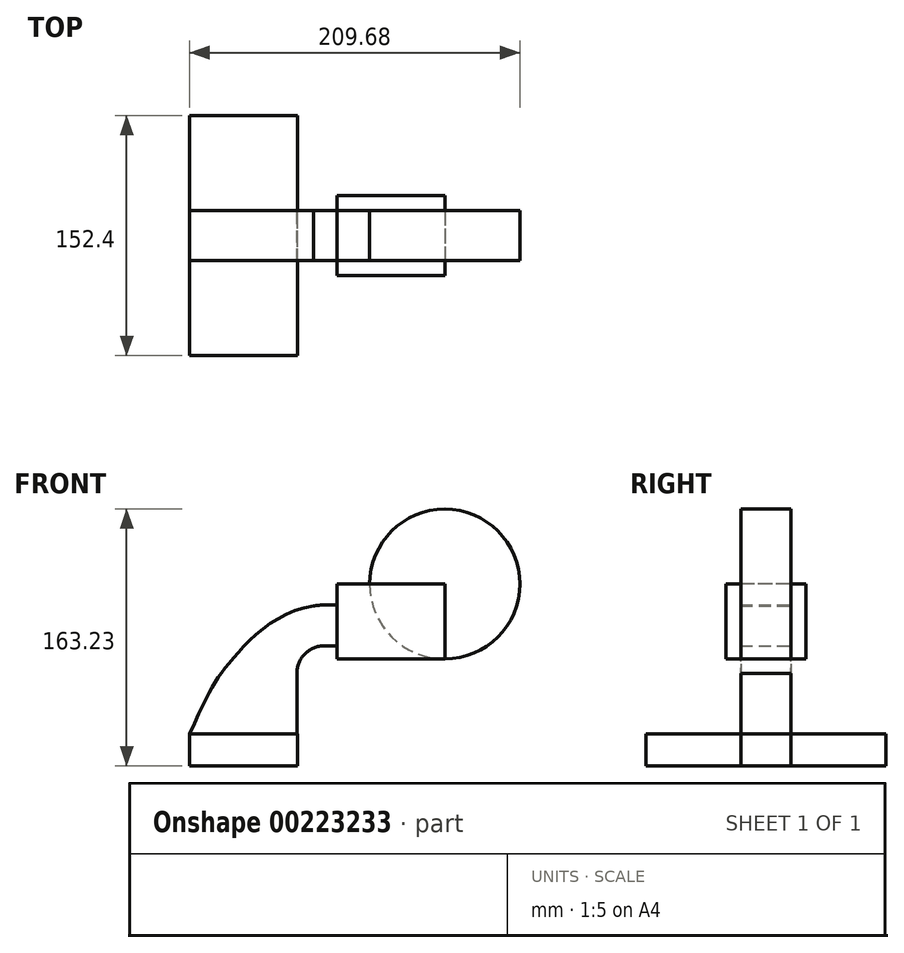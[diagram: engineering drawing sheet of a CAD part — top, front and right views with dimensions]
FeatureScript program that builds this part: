
annotation { "Feature Type Name" : "Feature", "Feature Type Description" : "" }
export const myFeature = defineFeature(function(context is Context, id is Id, definition is map)
    precondition{}
    {
        {
            var Q0;
            Q0=qCreatedBy(makeId("Front.planeOp"),FACE);
            var sketch = newSketch(context, id + "F0", { "sketchPlane" : qUnion([Q0])});
            skLineSegment(sketch, "E0.bottom", {"start": v(-34.2, -10.12) * mm, "end": v(34.2, -10.12) * mm});
            skLineSegment(sketch, "E0.top", {"start": v(-34.2, 10.12) * mm, "end": v(34.2, 10.12) * mm});
            skLineSegment(sketch, "E0.left", {"start": v(-34.2, -10.12) * mm, "end": v(-34.2, 10.12) * mm});
            skLineSegment(sketch, "E0.right", {"start": v(34.2, -10.12) * mm, "end": v(34.2, 10.12) * mm});
            skPoint(sketch, "E0.middle", {"position": v(0, 0) * mm});
            skLineSegment(sketch, "E1.bottom", {"start": v(59.33, 57.79) * mm, "end": v(127.8, 57.79) * mm});
            skLineSegment(sketch, "E1.top", {"start": v(59.33, 105.45) * mm, "end": v(127.8, 105.45) * mm});
            skLineSegment(sketch, "E1.left", {"start": v(59.33, 57.79) * mm, "end": v(59.33, 105.45) * mm});
            skLineSegment(sketch, "E1.right", {"start": v(127.8, 57.79) * mm, "end": v(127.8, 105.45) * mm});
            skPoint(sketch, "E1.middle", {"position": v(93.57, 81.62) * mm});
            skLineSegment(sketch, "E2", {"start": v(33.94, 10.12) * mm, "end": v(33.94, 48.61) * mm});
            skArc(sketch, "E3", {"start": v(33.94, 48.61) * mm, "mid": v(38.94, 61.05) * mm, "end": v(51.33, 66.16) * mm});
            skLineSegment(sketch, "E4", {"start": v(51.33, 66.16) * mm, "end": v(62.73, 66.16) * mm});
            skLineSegment(sketch, "E5.0", {"start": v(51, 92.07) * mm, "end": v(59.33, 92.07) * mm});
            skArc(sketch, "E5.1", {"start": v(8.03, 48.44) * mm, "mid": v(20.44, 79.2) * mm, "end": v(51, 92.07) * mm});
            skLineSegment(sketch, "E5.2", {"start": v(8.03, 10.12) * mm, "end": v(8.03, 48.44) * mm});
            skFitSpline(sketch, "E6", {"points": [v(-34.2, 10.12) * mm, v(-8.92, 55.48) * mm, v(51, 92.07) * mm], "startDerivative": vector(76.74, 174.65) * mm, "endDerivative": vector(157, 3.34) * mm});
            skSolve(sketch);
        }
        {
            var Q0;
            Q0=makeQuery(id+"F0.imprint","IMPRINT",FACE,{"disambiguationData":[TD([[makeQuery(id+"F0.imprint","IMPRINT",EDGE,{"derivedFrom":sQuery(id+"F0.wireOp",EDGE,"E0.bottom")}),1.0]])]});
            extrude(context, id + "F1", {"entities" : qUnion([Q0]), "endBound" : BoundingType.SYMMETRIC, "depth" : 152.4 * mm});
        }
        {
            var Q0;
            {var subQ3=sQuery(id+"F0.wireOp",EDGE,"E1.bottom");Q0=makeQuery(id+"F0.imprint","IMPRINT",FACE,{"disambiguationData":[TD([[makeQuery(id+"F0.imprint","IMPRINT",EDGE,{"derivedFrom":subQ3}),1.0]])]});}
            extrude(context, id + "F2", {"entities" : qUnion([Q0]), "endBound" : BoundingType.SYMMETRIC, "oppositeDirection" : true, "depth" : 50.8 * mm});
        }
        {
            var Q0;
            Q0 = qSketchRegion(id + "F0", true);
            extrude(context, id + "F3", {"entities" : qUnion([Q0]), "endBound" : BoundingType.SYMMETRIC, "depth" : 31.75 * mm});
        }
        {
            var Q0;
            Q0=makeQuery(id+"F3.opExtrude","SWEPT_FACE",FACE,{"disambiguationData":[OSD([sQuery(id+"F0.wireOp",EDGE,"E1.right")])]});
            var Q1;
            Q1=makeQuery(id+"F3.opExtrude","SWEPT_EDGE",EDGE,{"disambiguationData":[OSD([sQuery(id+"F0.wireOp",EDGE,"E1.top"),sQuery(id+"F0.wireOp",EDGE,"E1.right")])]});
            revolve(context, id + "F4", {"entities" : qUnion([Q0]), "axis" : qUnion([Q1]), "revolveType" : RevolveType.FULL});
        }
    });
